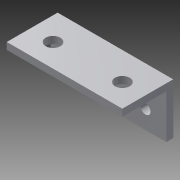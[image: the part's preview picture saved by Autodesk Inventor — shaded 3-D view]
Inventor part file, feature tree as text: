
AUTODESK INVENTOR PART (.ipt)
format: ipt  version: 2015 (Build 190159000, 159)  size: 141,312 bytes
history: native  units: mm
features: sketch x6, extrude x4, hole x2, other x1
ambient origin geometry x8: Origin, YZ Plane, XZ Plane, XY Plane, X Axis, Y Axis, Z Axis, Center Point
bodies: Body1 (feature_tree)
feature tree (13):
  other  "ソリッド1"
  extrude  "押し出し1"  Depth=25.0mm
  extrude  "押し出し2"  Depth=10.0mm
  extrude  "押し出し4"  Depth=1.0mm TaperAngle=0.0deg
  extrude  "押し出し5"  Depth=25.0mm
  hole  "穴3"  [1 undecoded]
  hole  "穴4"  [1 undecoded]
  sketch  "スケッチ1"
  sketch  "スケッチ3"
  sketch  "スケッチ7"
  sketch  "スケッチ8"
  sketch  "スケッチ9"
  sketch  "スケッチ10"
note: 2 required parameter values undecoded (feature->parameter linkage not recoverable at this tier; creation-order binding heuristic only, values carry confidence <= 0.55)
